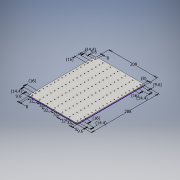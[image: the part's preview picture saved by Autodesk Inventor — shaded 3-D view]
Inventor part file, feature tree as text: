
AUTODESK INVENTOR PART (.ipt)
format: ipt  version: 2016 (Build 200138000, 138)  size: 273,408 bytes
history: native  units: mm
features: reference x112, extrude x1, sketch x1
ambient origin geometry x8: Origin, YZ Plane, XZ Plane, XY Plane, X Axis, Y Axis, Z Axis, Center Point
bodies: Body1 (feature_tree)
feature tree (114):
  extrude  "Extrusion8"  Depth=4.0mm
  sketch  "Sketch1"  dims[d0=208.0mm d1=288.0mm d17=32.0mm d18=32.0mm d19=32.0mm d20=32.0mm d21=32.0mm d22=32.0mm d23=8.0mm d25=9.6mm d26=9.6mm d27=8.0mm d29=9.6mm d30=8.0mm d31=14.4mm d32=16.0mm d33=14.4mm d34=14.4mm d35=16.0mm d36=14.4mm d37=16.0mm d38=16.0mm d39=9.6mm d40=8.0mm d41=4.0mm d42=0.0mm]
  reference  "Reference4"
  reference  "Reference8"
  reference  "Reference9"
  reference  "Reference10"
  reference  "Reference11"
  reference  "Reference12"
  reference  "Reference13"
  reference  "Reference14"
  reference  "Reference15"
  reference  "Reference16"
  reference  "Reference17"
  reference  "Reference18"
  reference  "Reference19"
  reference  "Reference20"
  reference  "Reference21"
  reference  "Reference22"
  reference  "Reference23"
  reference  "Reference24"
  reference  "Reference25"
  reference  "Reference26"
  reference  "Reference27"
  reference  "Reference28"
  reference  "Reference29"
  reference  "Reference30"
  reference  "Reference31"
  reference  "Reference32"
  reference  "Reference33"
  reference  "Reference34"
  reference  "Reference35"
  reference  "Reference36"
  reference  "Reference37"
  reference  "Reference38"
  reference  "Reference39"
  reference  "Reference40"
  reference  "Reference41"
  reference  "Reference42"
  reference  "Reference43"
  reference  "Reference44"
  reference  "Reference45"
  reference  "Reference46"
  reference  "Reference47"
  reference  "Reference48"
  reference  "Reference49"
  reference  "Reference50"
  reference  "Reference51"
  reference  "Reference52"
  reference  "Reference53"
  reference  "Reference54"
  reference  "Reference55"
  reference  "Reference56"
  reference  "Reference57"
  reference  "Reference58"
  reference  "Reference59"
  reference  "Reference60"
  reference  "Reference61"
  reference  "Reference62"
  reference  "Reference63"
  reference  "Reference64"
  reference  "Reference65"
  reference  "Reference66"
  reference  "Reference67"
  reference  "Reference68"
  reference  "Reference69"
  reference  "Reference70"
  reference  "Reference71"
  reference  "Reference72"
  reference  "Reference73"
  reference  "Reference74"
  reference  "Reference75"
  reference  "Reference76"
  reference  "Reference77"
  reference  "Reference78"
  reference  "Reference79"
  reference  "Reference80"
  reference  "Reference81"
  reference  "Reference82"
  reference  "Reference83"
  reference  "Reference84"
  reference  "Reference85"
  reference  "Reference86"
  reference  "Reference87"
  reference  "Reference88"
  reference  "Reference89"
  reference  "Reference90"
  reference  "Reference91"
  reference  "Reference92"
  reference  "Reference93"
  reference  "Reference94"
  reference  "Reference95"
  reference  "Reference96"
  reference  "Reference97"
  reference  "Reference98"
  reference  "Reference99"
  reference  "Reference100"
  reference  "Reference101"
  reference  "Reference102"
  reference  "Reference103"
  reference  "Reference104"
  reference  "Reference105"
  reference  "Reference106"
  reference  "Reference107"
  reference  "Reference108"
  reference  "Reference109"
  reference  "Reference110"
  reference  "Reference111"
  reference  "Reference112"
  reference  "Reference113"
  reference  "Reference114"
  reference  "Reference115"
  reference  "Reference116"
  reference  "Reference117"
  reference  "Reference118"
